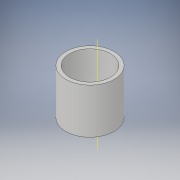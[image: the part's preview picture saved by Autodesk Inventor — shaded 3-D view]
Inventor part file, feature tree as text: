
AUTODESK INVENTOR PART (.ipt)
format: ipt  version: 2017 (Build 210142000, 142)  size: 139,264 bytes
history: native  units: in
note: dims shown in document units (in); Inventor stores cm internally (conversion verified against a paired STEP export)
features: sketch x1, other x1, revolve x1
ambient origin geometry x8: Origin, YZ Plane, XZ Plane, XY Plane, X Axis, Y Axis, Z Axis, Center Point
bodies: Body1 (feature_tree)
feature tree (3):
  sketch  "Sketch1"  dims[d0=0.25in d2=15.0deg d3=0.1718in d4=0.25in d5=1.5in d6=0.25in d7=0.25in d11=0.125in d15=0.125in d16=0.125in d18=0.375in d20=0.125in d22=0.125in d23=0.1718in d24=0.125in d25=0.5in d26=0.0625in d27=0.0667in d28=0.125in d29=0.125in d30=0.5in d31=0.125in d32=0.5in d34=90.0deg]
  other  "Work Axis1"
  revolve  "Revolution2"  Angle=15.0deg
